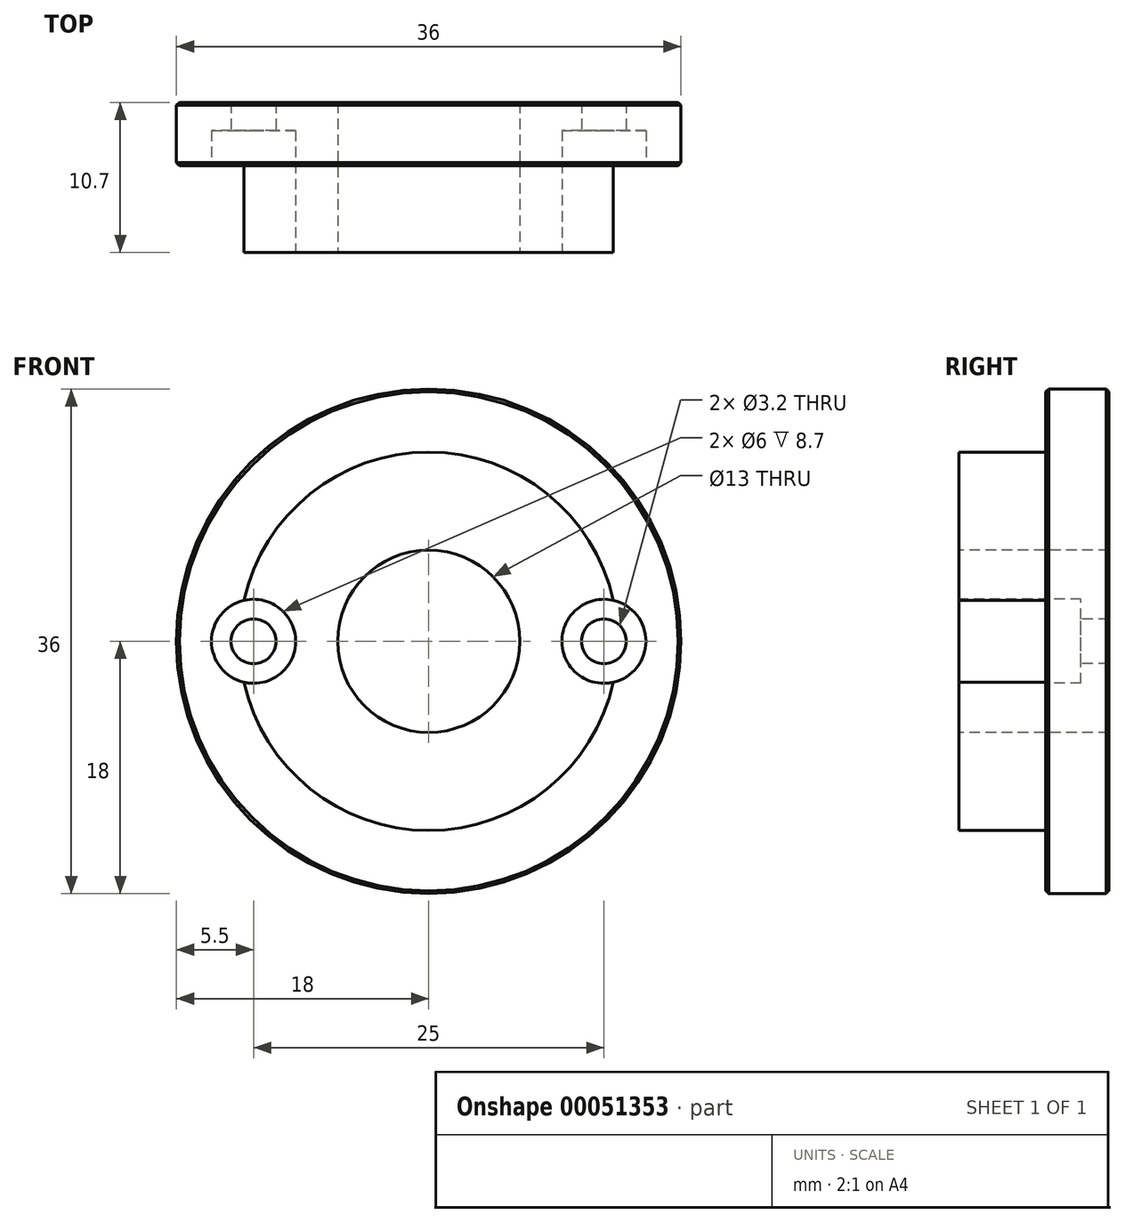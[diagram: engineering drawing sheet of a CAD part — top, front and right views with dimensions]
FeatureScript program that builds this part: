
annotation { "Feature Type Name" : "Feature", "Feature Type Description" : "" }
export const myFeature = defineFeature(function(context is Context, id is Id, definition is map)
    precondition{}
    {
        {
            var Q0;
            Q0=qCreatedBy(makeId("Front.planeOp"),FACE);
            var sketch = newSketch(context, id + "F0", { "sketchPlane" : qUnion([Q0])});
            skCircle(sketch, "E0", {"center": v(0, 0) * mm, "radius": 18 * mm});
            skCircle(sketch, "E1", {"center": v(0, 0) * mm, "radius": 12.5 * mm, "construction": true});
            skCircle(sketch, "E2", {"center": v(0, 0) * mm, "radius": 6.5 * mm});
            skLineSegment(sketch, "E3", {"start": v(-19.16, 0) * mm, "end": v(21.52, 0) * mm, "construction": true});
            skCircle(sketch, "E4", {"center": v(-12.5, 0) * mm, "radius": 1.6 * mm});
            skCircle(sketch, "E5.1.0", {"center": v(12.5, 0) * mm, "radius": 1.6 * mm});
            skSolve(sketch);
        }
        {
            var Q0;
            Q0 = qSketchRegion(id + "F0", true);
            extrude(context, id + "F1", {"entities" : qUnion([Q0]), "oppositeDirection" : true, "depth" : 4.5 * mm});
        }
        {
            var Q0;
            Q0=makeQuery(id+"F1.opExtrude","CAP_EDGE",EDGE,{"disambiguationData":[OSD([sQuery(id+"F0.wireOp",EDGE,"E0")])],"isStart":false});
            var Q1;
            Q1=makeQuery(id+"F1.opExtrude","CAP_EDGE",EDGE,{"disambiguationData":[OSD([sQuery(id+"F0.wireOp",EDGE,"E0")])],"isStart":true});
            chamfer(context, id + "F2", {"entities" : qUnion([Q0, Q1]), "width" : 0.2 * mm, "tangentPropagation" : true});
        }
        {
            var Q0;
            Q0=makeQuery(id+"F1.opExtrude","CAP_FACE",FACE,{"disambiguationData":[OSD([sQuery(id+"F0.wireOp",EDGE,"E0"),sQuery(id+"F0.wireOp",EDGE,"E2"),sQuery(id+"F0.wireOp",EDGE,"E4"),sQuery(id+"F0.wireOp",EDGE,"E5.1.0")])],"isStart":true});
            var sketch = newSketch(context, id + "F3", { "sketchPlane" : qUnion([Q0])});
            skCircle(sketch, "E6.0", {"center": v(0, 0) * mm, "radius": 6.5 * mm});
            skArc(sketch, "E7", {"start": v(-13.44, -1.3) * mm, "mid": v(0, -13.5) * mm, "end": v(13.44, -1.3) * mm});
            skArc(sketch, "E8.0", {"start": v(-13.44, -1.3) * mm, "mid": v(-10.9, 0) * mm, "end": v(-13.44, 1.3) * mm});
            skArc(sketch, "E9.0", {"start": v(13.44, 1.3) * mm, "mid": v(10.9, 0) * mm, "end": v(13.44, -1.3) * mm});
            skArc(sketch, "E10.trimOffspring", {"start": v(13.44, 1.3) * mm, "mid": v(0, 13.5) * mm, "end": v(-13.44, 1.3) * mm});
            skSolve(sketch);
        }
        {
            var Q0;
            Q0 = qSketchRegion(id + "F3", true);
            extrude(context, id + "F4", {"entities" : qUnion([Q0]), "operationType" : NewBodyOperationType.ADD, "depth" : (10.7 - 4.5) * mm});
        }
        {
            var Q0;
            Q0=makeQuery(id+"F1.opExtrude","CAP_FACE",FACE,{"disambiguationData":[OSD([sQuery(id+"F0.wireOp",EDGE,"E0"),sQuery(id+"F0.wireOp",EDGE,"E2"),sQuery(id+"F0.wireOp",EDGE,"E4"),sQuery(id+"F0.wireOp",EDGE,"E5.1.0")])],"isStart":true});
            var sketch = newSketch(context, id + "F5", { "sketchPlane" : qUnion([Q0])});
            skCircle(sketch, "E11.0", {"center": v(-12.5, 0) * mm, "radius": 1.6 * mm, "construction": true});
            skCircle(sketch, "E12.0", {"center": v(12.5, 0) * mm, "radius": 1.6 * mm, "construction": true});
            skCircle(sketch, "E13", {"center": v(-12.5, 0) * mm, "radius": 3 * mm});
            skCircle(sketch, "E14.1.0", {"center": v(12.5, 0) * mm, "radius": 3 * mm});
            skPoint(sketch, "E14.center", {"position": v(0, 0) * mm});
            skSolve(sketch);
        }
        {
            var Q0;
            Q0 = qSketchRegion(id + "F5", true);
            extrude(context, id + "F6", {"entities" : qUnion([Q0]), "operationType" : NewBodyOperationType.REMOVE, "oppositeDirection" : true, "depth" : (4.5 - 2) * mm, "hasSecondDirection" : true, "secondDirectionBound" : BoundingType.THROUGH_ALL, "secondDirectionOppositeDirection" : false, "secondDirectionDepth" : 25 * mm});
        }
    });
